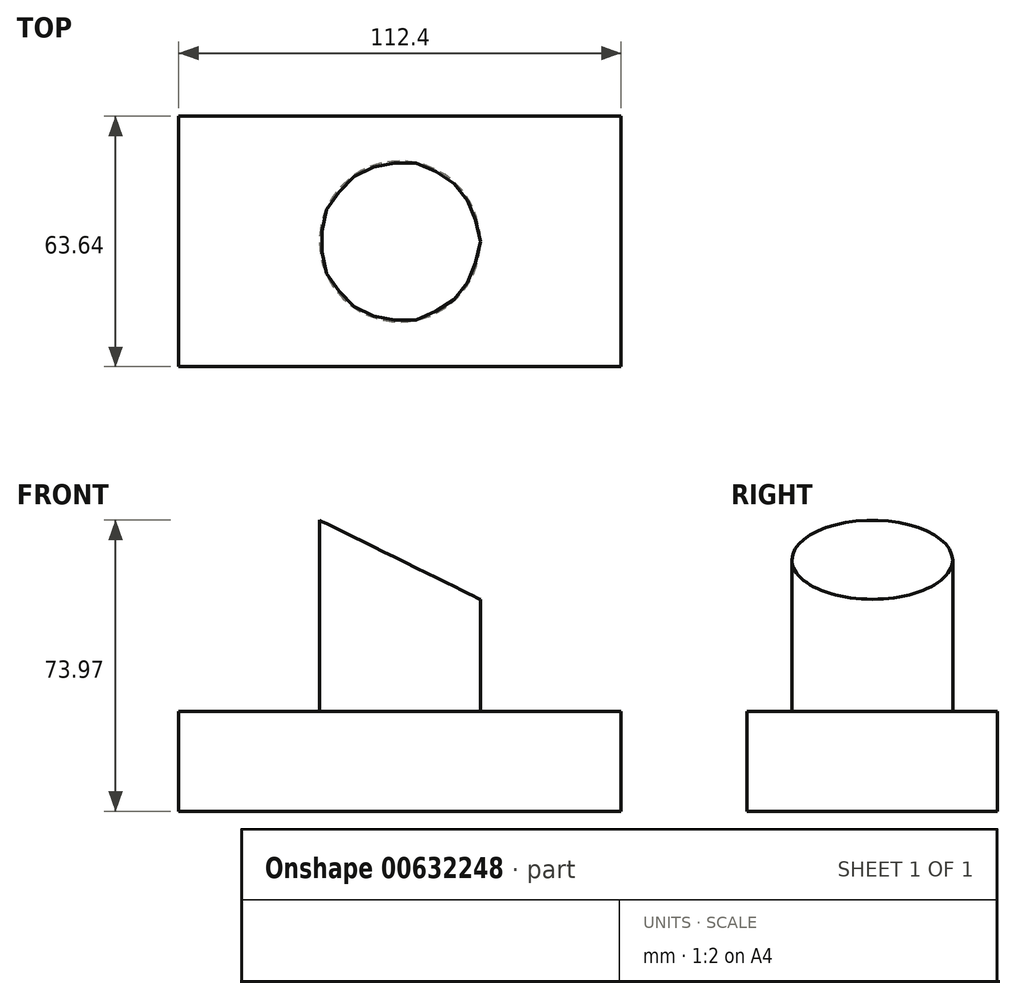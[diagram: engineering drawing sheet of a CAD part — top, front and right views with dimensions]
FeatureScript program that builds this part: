
annotation { "Feature Type Name" : "Feature", "Feature Type Description" : "" }
export const myFeature = defineFeature(function(context is Context, id is Id, definition is map)
    precondition{}
    {
        {
            var Q0;
            Q0=qCreatedBy(makeId("Top.planeOp"),FACE);
            var sketch = newSketch(context, id + "F0", { "sketchPlane" : qUnion([Q0])});
            skLineSegment(sketch, "E0.bottom", {"start": v(-56.2, 31.82) * mm, "end": v(56.2, 31.82) * mm});
            skLineSegment(sketch, "E0.top", {"start": v(-56.2, -31.82) * mm, "end": v(56.2, -31.82) * mm});
            skLineSegment(sketch, "E0.left", {"start": v(-56.2, 31.82) * mm, "end": v(-56.2, -31.82) * mm});
            skLineSegment(sketch, "E0.right", {"start": v(56.2, 31.82) * mm, "end": v(56.2, -31.82) * mm});
            skPoint(sketch, "E0.middle", {"position": v(0, 0) * mm});
            skSolve(sketch);
        }
        {
            var Q0;
            Q0 = qSketchRegion(id + "F0", true);
            extrude(context, id + "F1", {"entities" : qUnion([Q0]), "depth" : 25.4 * mm, "offsetDistance" : 25.4 * mm});
        }
        {
            var Q0;
            Q0=makeQuery(id+"F1.opExtrude","CAP_FACE",FACE,{"disambiguationData":[OSD([sQuery(id+"F0.wireOp",EDGE,"E0.bottom"),sQuery(id+"F0.wireOp",EDGE,"E0.top"),sQuery(id+"F0.wireOp",EDGE,"E0.left"),sQuery(id+"F0.wireOp",EDGE,"E0.right")])],"isStart":false});
            var sketch = newSketch(context, id + "F2", { "sketchPlane" : qUnion([Q0])});
            skCircle(sketch, "E1", {"center": v(0, 0) * mm, "radius": 20.43 * mm});
            skSolve(sketch);
        }
        {
            var Q0;
            Q0 = qSketchRegion(id + "F2", true);
            extrude(context, id + "F3", {"entities" : qUnion([Q0]), "operationType" : NewBodyOperationType.ADD, "depth" : 50.8 * mm, "offsetDistance" : 25.4 * mm});
        }
        {
            var Q0;
            Q0=qCreatedBy(makeId("Front.planeOp"),FACE);
            var sketch = newSketch(context, id + "F4", { "sketchPlane" : qUnion([Q0])});
            skLineSegment(sketch, "E2", {"start": v(-34.63, 80.95) * mm, "end": v(42.32, 80.95) * mm});
            skLineSegment(sketch, "E3", {"start": v(42.32, 80.95) * mm, "end": v(42.32, 43.1) * mm});
            skLineSegment(sketch, "E4", {"start": v(42.32, 43.1) * mm, "end": v(-34.63, 80.95) * mm});
            skSolve(sketch);
        }
        {
            var Q0;
            Q0 = qSketchRegion(id + "F4", true);
            extrude(context, id + "F5", {"entities" : qUnion([Q0]), "operationType" : NewBodyOperationType.REMOVE, "endBound" : BoundingType.SYMMETRIC, "depth" : 50.8 * mm, "offsetDistance" : 25.4 * mm});
        }
    });
